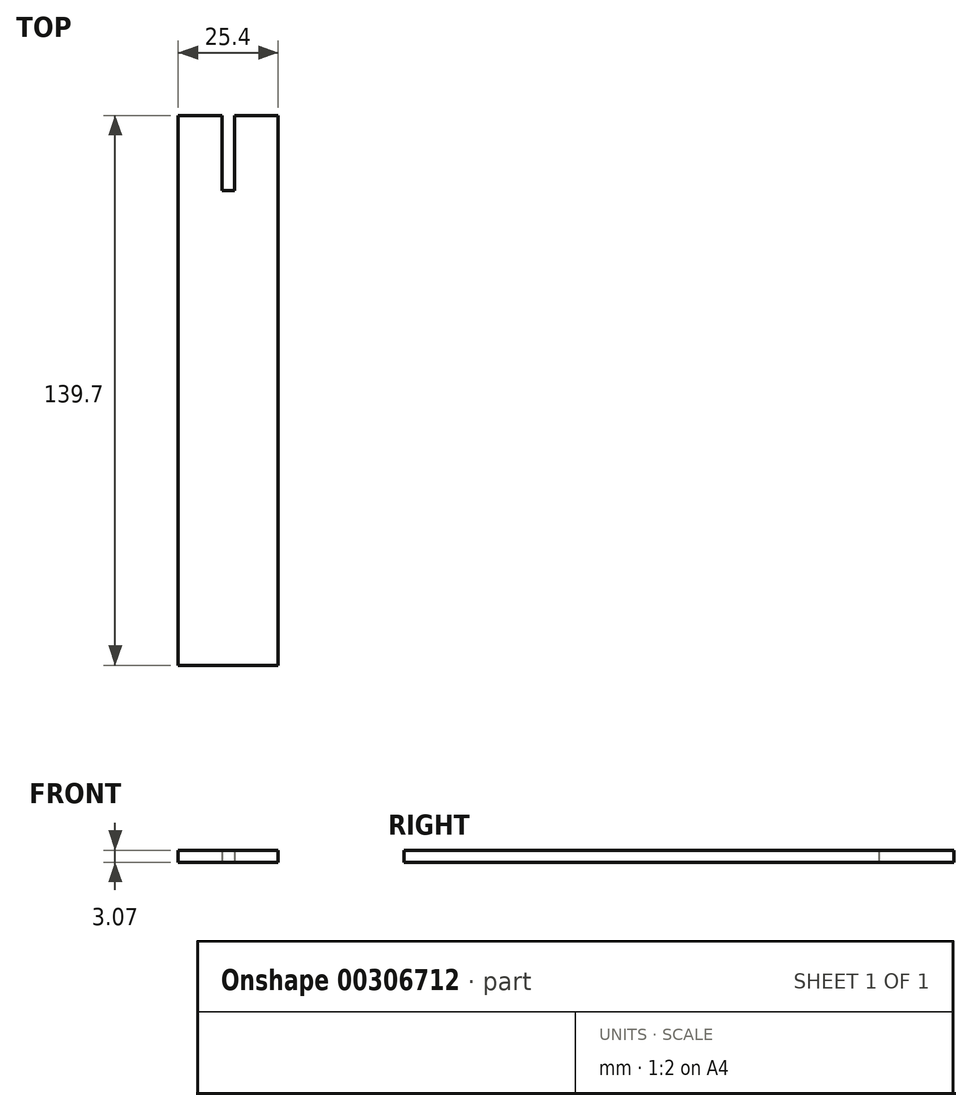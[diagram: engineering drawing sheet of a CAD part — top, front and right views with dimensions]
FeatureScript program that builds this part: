
annotation { "Feature Type Name" : "Feature", "Feature Type Description" : "" }
export const myFeature = defineFeature(function(context is Context, id is Id, definition is map)
    precondition{}
    {
        {
            var Q0;
            Q0=qCreatedBy(makeId("Top.planeOp"),FACE);
            var sketch = newSketch(context, id + "F0", { "sketchPlane" : qUnion([Q0])});
            skLineSegment(sketch, "E0.top", {"start": v(-122.8, -129.35) * mm, "end": v(-97.4, -129.35) * mm});
            skLineSegment(sketch, "E0.left", {"start": v(-122.8, 10.35) * mm, "end": v(-122.8, -129.35) * mm});
            skLineSegment(sketch, "E0.right", {"start": v(-97.4, 10.35) * mm, "end": v(-97.4, -129.35) * mm});
            skLineSegment(sketch, "E1.top", {"start": v(-111.68, -8.7) * mm, "end": v(-108.5, -8.7) * mm});
            skLineSegment(sketch, "E1.left", {"start": v(-111.68, 10.35) * mm, "end": v(-111.68, -8.7) * mm});
            skLineSegment(sketch, "E1.right", {"start": v(-108.5, 10.35) * mm, "end": v(-108.5, -8.7) * mm});
            skLineSegment(sketch, "E2", {"start": v(-122.8, 10.35) * mm, "end": v(-111.68, 10.35) * mm});
            skLineSegment(sketch, "E3", {"start": v(-108.5, 10.35) * mm, "end": v(-97.4, 10.35) * mm});
            skSolve(sketch);
        }
        {
            var Q0;
            Q0=makeQuery(id+"F0.imprint","IMPRINT",FACE,{"disambiguationData":[TD([[makeQuery(id+"F0.imprint","IMPRINT",EDGE,{"derivedFrom":sQuery(id+"F0.wireOp",EDGE,"E0.top")}),1.0]])]});
            extrude(context, id + "F1", {"entities" : qUnion([Q0]), "depth" : 3.07 * mm});
        }
    });
